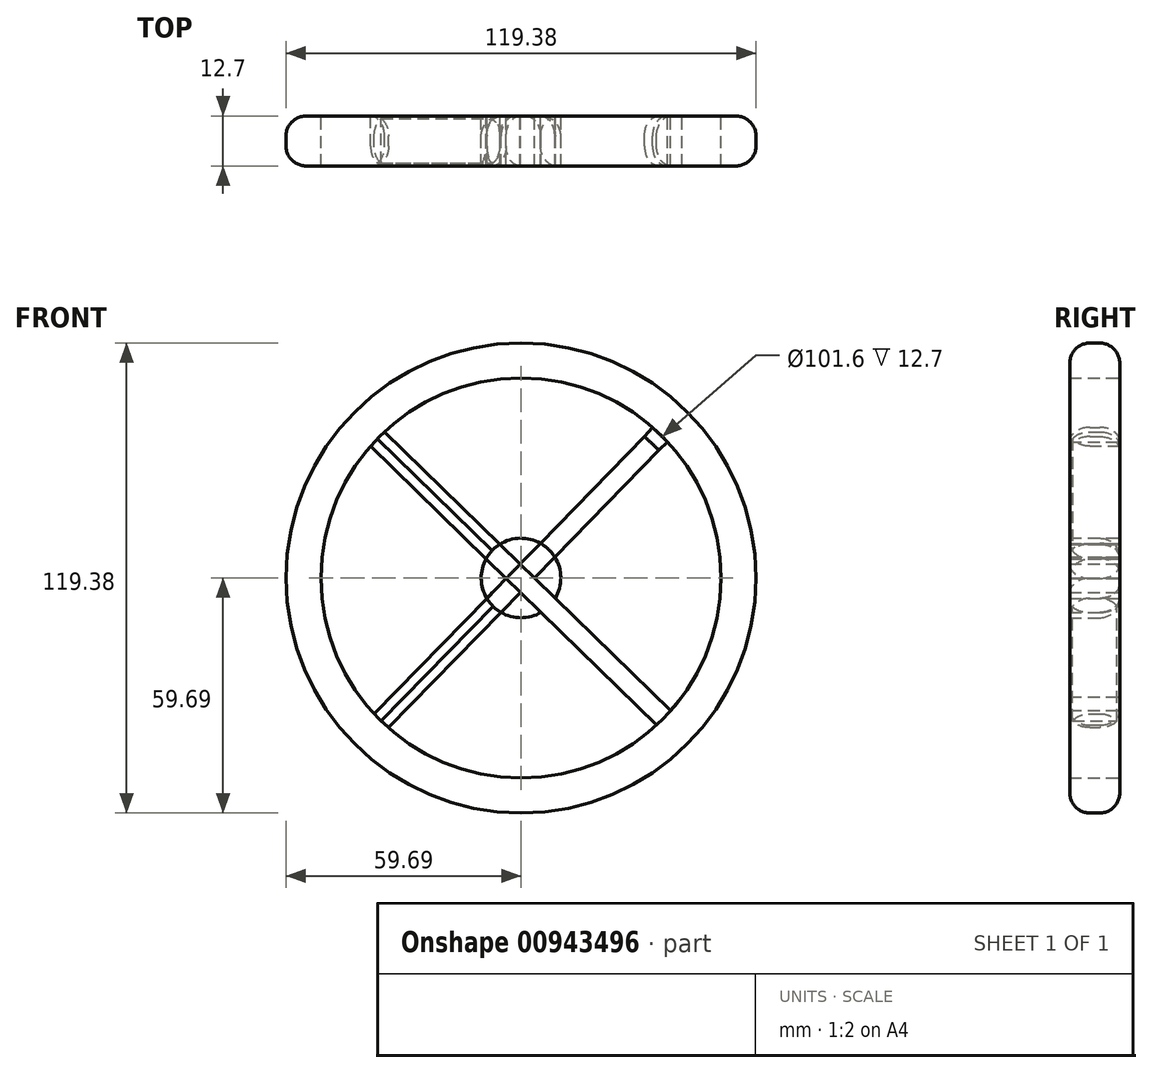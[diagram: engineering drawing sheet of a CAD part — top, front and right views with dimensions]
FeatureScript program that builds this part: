
annotation { "Feature Type Name" : "Feature", "Feature Type Description" : "" }
export const myFeature = defineFeature(function(context is Context, id is Id, definition is map)
    precondition{}
    {
        {
            var Q0;
            Q0=qCreatedBy(makeId("Front.planeOp"),FACE);
            var sketch = newSketch(context, id + "F0", { "sketchPlane" : qUnion([Q0])});
            skCircle(sketch, "E0", {"center": v(0, 0) * mm, "radius": 50.8 * mm});
            skCircle(sketch, "E1.0", {"center": v(0, 0) * mm, "radius": 59.7 * mm});
            skCircle(sketch, "E2", {"center": v(0, 0) * mm, "radius": 10.1 * mm});
            skLineSegment(sketch, "E3", {"start": v(37.18, 34.62) * mm, "end": v(-33.62, -38) * mm});
            skLineSegment(sketch, "E4", {"start": v(34.44, -37.34) * mm, "end": v(-38.2, 33.48) * mm});
            skLineSegment(sketch, "E5", {"start": v(31.36, 35.93) * mm, "end": v(-37.3, -34.5) * mm});
            skLineSegment(sketch, "E6", {"start": v(37.98, -33.7) * mm, "end": v(-34.67, 37.13) * mm});
            skLineSegment(sketch, "E7", {"start": v(-31.35, 38.6) * mm, "end": v(-34.67, 35.66) * mm});
            skLineSegment(sketch, "E8", {"start": v(40.85, -30.2) * mm, "end": v(37.98, -33.7) * mm});
            skLineSegment(sketch, "E9", {"start": v(37.02, 34.7) * mm, "end": v(37.18, 34.53) * mm});
            skLineSegment(sketch, "E10", {"start": v(-31.71, -39.69) * mm, "end": v(-35.52, -36.32) * mm});
            skPoint(sketch, "E11", {"position": v(-33.01, 37.13) * mm});
            skPoint(sketch, "E12", {"position": v(37.1, 34.62) * mm});
            skLineSegment(sketch, "E13", {"start": v(31.36, 35.93) * mm, "end": v(33.4, 38.27) * mm});
            skLineSegment(sketch, "E14", {"start": v(33.4, 38.27) * mm, "end": v(37.18, 34.62) * mm});
            skSolve(sketch);
        }
        {
            var Q0;
            Q0=makeQuery(id+"F0.imprint","IMPRINT",FACE,{"disambiguationData":[TD([[makeQuery(id+"F0.imprint","IMPRINT",EDGE,{"derivedFrom":sQuery(id+"F0.wireOp",EDGE,"E0")}),-1.0]])]});
            extrude(context, id + "F1", {"entities" : qUnion([Q0]), "endBound" : BoundingType.SYMMETRIC, "depth" : 12.7 * mm, "offsetDistance" : 25.4 * mm});
        }
        {
            var Q0;
            Q0=makeQuery(id+"F1.opExtrude","CAP_EDGE",EDGE,{"disambiguationData":[OSD([sQuery(id+"F0.wireOp",EDGE,"E1.0")])],"isStart":true});
            var Q1;
            Q1=makeQuery(id+"F1.opExtrude","CAP_EDGE",EDGE,{"disambiguationData":[OSD([sQuery(id+"F0.wireOp",EDGE,"E1.0")])],"isStart":false});
            fillet(context, id + "F2", {"entities" : qUnion([Q0, Q1]), "radius" : 5.08 * mm, "tangentPropagation" : true, "allowEdgeOverflow" : false});
        }
        {
            var Q0;
            Q0=makeQuery(id+"F0.imprint","IMPRINT",FACE,{"disambiguationData":[TD([[makeQuery(id+"F0.imprint","IMPRINT",EDGE,{"derivedFrom":sQuery(id+"F0.wireOp",EDGE,"E2")}),1.0]])]});
            extrude(context, id + "F3", {"entities" : qUnion([Q0]), "endBound" : BoundingType.SYMMETRIC, "depth" : 12.7 * mm, "offsetDistance" : 25.4 * mm});
        }
        {
            var Q0;
            Q0=makeQuery(id+"F3.opExtrude","CAP_EDGE",EDGE,{"disambiguationData":[OSD([sQuery(id+"F0.wireOp",EDGE,"E2")])],"isStart":true});
            fillet(context, id + "F4", {"entities" : qUnion([Q0]), "radius" : 5.08 * mm, "tangentPropagation" : true, "allowEdgeOverflow" : false});
        }
        {
            var Q0;
            {var subQ0=sQuery(id+"F0.wireOp",EDGE,"E8");Q0=makeQuery(id+"F0.imprint","IMPRINT",FACE,{"disambiguationData":[TD([[makeQuery(id+"F0.imprint","IMPRINT",EDGE,{"derivedFrom":subQ0}),1.0]])]});}
            var Q1;
            {var subQ0=sQuery(id+"F0.wireOp",EDGE,"E4");var subQ1=sQuery(id+"F0.wireOp",EDGE,"E2");var subQ2=makeQuery(id+"F0.imprint","INTERSECT",VERTEX,{"disambiguationData":[OD(1.0)],"derivedFrom":[subQ1,subQ0]});Q1=makeQuery(id+"F0.imprint","IMPRINT",FACE,{"disambiguationData":[TD([[makeQuery(id+"F0.imprint","IMPRINT",EDGE,{"disambiguationData":[TD([[subQ2,-1.0]])],"derivedFrom":subQ1}),1.0]])]});}
            var Q2;
            {var subQ0=sQuery(id+"F0.wireOp",EDGE,"E6");var subQ1=sQuery(id+"F0.wireOp",EDGE,"E3");var subQ2=makeQuery(id+"F0.imprint","INTERSECT",VERTEX,{"derivedFrom":[subQ1,subQ0]});Q2=makeQuery(id+"F0.imprint","IMPRINT",FACE,{"disambiguationData":[TD([[makeQuery(id+"F0.imprint","IMPRINT",EDGE,{"disambiguationData":[TD([[subQ2,-1.0]])],"derivedFrom":subQ1}),-1.0]])]});}
            var Q3;
            {var subQ0=sQuery(id+"F0.wireOp",EDGE,"E6");var subQ1=makeQuery(id+"F0.imprint","IMPRINT",VERTEX,{"derivedFrom":subQ0});Q3=makeQuery(id+"F0.imprint","IMPRINT",FACE,{"disambiguationData":[TD([[makeQuery(id+"F0.imprint","IMPRINT",EDGE,{"disambiguationData":[TD([[subQ1,1.0]])],"derivedFrom":subQ0}),1.0]])]});}
            var Q4;
            {var subQ0=sQuery(id+"F0.wireOp",EDGE,"E6");var subQ1=sQuery(id+"F0.wireOp",EDGE,"E2");var subQ2=makeQuery(id+"F0.imprint","INTERSECT",VERTEX,{"disambiguationData":[OD(0.0)],"derivedFrom":[subQ1,subQ0]});Q4=makeQuery(id+"F0.imprint","IMPRINT",FACE,{"disambiguationData":[TD([[makeQuery(id+"F0.imprint","IMPRINT",EDGE,{"disambiguationData":[TD([[subQ2,-1.0]])],"derivedFrom":subQ1}),1.0]])]});}
            var Q5;
            {var subQ0=sQuery(id+"F0.wireOp",EDGE,"E5");var subQ1=sQuery(id+"F0.wireOp",EDGE,"E0");var subQ2=makeQuery(id+"F0.imprint","INTERSECT",VERTEX,{"derivedFrom":[subQ1,subQ0]});Q5=makeQuery(id+"F0.imprint","IMPRINT",FACE,{"disambiguationData":[TD([[makeQuery(id+"F0.imprint","IMPRINT",EDGE,{"disambiguationData":[TD([[subQ2,-1.0]])],"derivedFrom":subQ1}),1.0]])]});}
            var Q6;
            {var subQ0=sQuery(id+"F0.wireOp",EDGE,"E5");var subQ1=sQuery(id+"F0.wireOp",EDGE,"E2");var subQ2=makeQuery(id+"F0.imprint","INTERSECT",VERTEX,{"disambiguationData":[OD(1.0)],"derivedFrom":[subQ1,subQ0]});Q6=makeQuery(id+"F0.imprint","IMPRINT",FACE,{"disambiguationData":[TD([[makeQuery(id+"F0.imprint","IMPRINT",EDGE,{"disambiguationData":[TD([[subQ2,-1.0]])],"derivedFrom":subQ1}),1.0]])]});}
            var Q7;
            {var subQ0=sQuery(id+"F0.wireOp",EDGE,"E13");Q7=makeQuery(id+"F0.imprint","IMPRINT",FACE,{"disambiguationData":[TD([[makeQuery(id+"F0.imprint","IMPRINT",EDGE,{"derivedFrom":subQ0}),-1.0]])]});}
            var Q8;
            {var subQ0=sQuery(id+"F0.wireOp",EDGE,"E5");var subQ1=sQuery(id+"F0.wireOp",EDGE,"E2");var subQ2=makeQuery(id+"F0.imprint","INTERSECT",VERTEX,{"disambiguationData":[OD(0.0)],"derivedFrom":[subQ1,subQ0]});Q8=makeQuery(id+"F0.imprint","IMPRINT",FACE,{"disambiguationData":[TD([[makeQuery(id+"F0.imprint","IMPRINT",EDGE,{"disambiguationData":[TD([[subQ2,1.0]])],"derivedFrom":subQ1}),1.0]])]});}
            extrude(context, id + "F5", {"entities" : qUnion([Q0, Q1, Q2, Q3, Q4, Q5, Q6, Q7, Q8]), "endBound" : BoundingType.SYMMETRIC, "depth" : 12.7 * mm, "offsetDistance" : 25.4 * mm});
        }
        {
            var Q0;
            {var subQ0=sQuery(id+"F0.wireOp",EDGE,"E4");var subQ1=makeQuery(id+"F0.imprint","INTERSECT",VERTEX,{"disambiguationData":[OD(1.0)],"derivedFrom":[sQuery(id+"F0.wireOp",EDGE,"E2"),subQ0]});Q0=makeQuery(id+"F5.opExtrude","CAP_EDGE",EDGE,{"disambiguationData":[OSD([subQ0]),TDD([makeQuery(id+"F0.imprint","IMPRINT",EDGE,{"disambiguationData":[TD([[makeQuery(id+"F0.imprint","INTERSECT",VERTEX,{"disambiguationData":[OD(0.0)],"derivedFrom":[sQuery(id+"F0.wireOp",EDGE,"E0"),subQ0]}),-1.0]])],"derivedFrom":subQ0}),makeQuery(id+"F0.imprint","IMPRINT",EDGE,{"disambiguationData":[TD([[subQ1,-1.0]])],"derivedFrom":subQ0})])],"isStart":false});}
            var Q1;
            {var subQ0=sQuery(id+"F0.wireOp",EDGE,"E3");var subQ1=makeQuery(id+"F0.imprint","INTERSECT",VERTEX,{"disambiguationData":[OD(1.0)],"derivedFrom":[sQuery(id+"F0.wireOp",EDGE,"E2"),subQ0]});Q1=makeQuery(id+"F5.opExtrude","CAP_EDGE",EDGE,{"disambiguationData":[OSD([subQ0]),TDD([makeQuery(id+"F0.imprint","IMPRINT",EDGE,{"disambiguationData":[TD([[subQ1,1.0]])],"derivedFrom":subQ0}),makeQuery(id+"F0.imprint","IMPRINT",EDGE,{"disambiguationData":[TD([[makeQuery(id+"F0.imprint","INTERSECT",VERTEX,{"derivedFrom":[subQ0,sQuery(id+"F0.wireOp",EDGE,"E10")]}),1.0]])],"derivedFrom":subQ0})])],"isStart":true});}
            var Q2;
            {var subQ0=sQuery(id+"F0.wireOp",EDGE,"E5");var subQ1=makeQuery(id+"F0.imprint","INTERSECT",VERTEX,{"disambiguationData":[OD(1.0)],"derivedFrom":[sQuery(id+"F0.wireOp",EDGE,"E2"),subQ0]});Q2=makeQuery(id+"F5.opExtrude","CAP_EDGE",EDGE,{"disambiguationData":[OSD([subQ0]),TDD([makeQuery(id+"F0.imprint","IMPRINT",EDGE,{"disambiguationData":[TD([[subQ1,1.0]])],"derivedFrom":subQ0}),makeQuery(id+"F0.imprint","IMPRINT",EDGE,{"disambiguationData":[TD([[makeQuery(id+"F0.imprint","INTERSECT",VERTEX,{"derivedFrom":[sQuery(id+"F0.wireOp",EDGE,"E0"),subQ0]}),1.0]])],"derivedFrom":subQ0})])],"isStart":false});}
            var Q3;
            {var subQ0=sQuery(id+"F0.wireOp",EDGE,"E5");var subQ1=makeQuery(id+"F0.imprint","INTERSECT",VERTEX,{"disambiguationData":[OD(0.0)],"derivedFrom":[sQuery(id+"F0.wireOp",EDGE,"E2"),subQ0]});Q3=makeQuery(id+"F5.opExtrude","CAP_EDGE",EDGE,{"disambiguationData":[OSD([subQ0]),TDD([makeQuery(id+"F0.imprint","IMPRINT",EDGE,{"disambiguationData":[TD([[makeQuery(id+"F0.imprint","INTERSECT",VERTEX,{"derivedFrom":[subQ0,sQuery(id+"F0.wireOp",EDGE,"E13")]}),-1.0]])],"derivedFrom":subQ0}),makeQuery(id+"F0.imprint","IMPRINT",EDGE,{"disambiguationData":[TD([[subQ1,-1.0]])],"derivedFrom":subQ0})])],"isStart":false});}
            var Q4;
            {var subQ0=sQuery(id+"F0.wireOp",EDGE,"E6");var subQ1=makeQuery(id+"F0.imprint","IMPRINT",VERTEX,{"derivedFrom":subQ0});var subQ2=makeQuery(id+"F0.imprint","INTERSECT",VERTEX,{"disambiguationData":[OD(0.0)],"derivedFrom":[sQuery(id+"F0.wireOp",EDGE,"E2"),subQ0]});Q4=makeQuery(id+"F5.opExtrude","CAP_EDGE",EDGE,{"disambiguationData":[OSD([subQ0]),TDD([makeQuery(id+"F0.imprint","IMPRINT",EDGE,{"disambiguationData":[TD([[subQ2,1.0]])],"derivedFrom":subQ0}),makeQuery(id+"F0.imprint","IMPRINT",EDGE,{"disambiguationData":[TD([[subQ1,1.0]])],"derivedFrom":subQ0}),makeQuery(id+"F0.imprint","IMPRINT",EDGE,{"disambiguationData":[TD([[subQ1,-1.0]])],"derivedFrom":subQ0})])],"isStart":false});}
            var Q5;
            {var subQ0=sQuery(id+"F0.wireOp",EDGE,"E4");var subQ1=makeQuery(id+"F0.imprint","INTERSECT",VERTEX,{"disambiguationData":[OD(0.0)],"derivedFrom":[sQuery(id+"F0.wireOp",EDGE,"E2"),subQ0]});Q5=makeQuery(id+"F5.opExtrude","CAP_EDGE",EDGE,{"disambiguationData":[OSD([subQ0]),TDD([makeQuery(id+"F0.imprint","IMPRINT",EDGE,{"disambiguationData":[TD([[subQ1,1.0]])],"derivedFrom":subQ0}),makeQuery(id+"F0.imprint","IMPRINT",EDGE,{"disambiguationData":[TD([[makeQuery(id+"F0.imprint","INTERSECT",VERTEX,{"disambiguationData":[OD(1.0)],"derivedFrom":[sQuery(id+"F0.wireOp",EDGE,"E0"),subQ0]}),1.0]])],"derivedFrom":subQ0})])],"isStart":false});}
            var Q6;
            {var subQ0=sQuery(id+"F0.wireOp",EDGE,"E4");var subQ1=makeQuery(id+"F0.imprint","INTERSECT",VERTEX,{"disambiguationData":[OD(1.0)],"derivedFrom":[sQuery(id+"F0.wireOp",EDGE,"E2"),subQ0]});Q6=makeQuery(id+"F5.opExtrude","CAP_EDGE",EDGE,{"disambiguationData":[OSD([subQ0]),TDD([makeQuery(id+"F0.imprint","IMPRINT",EDGE,{"disambiguationData":[TD([[makeQuery(id+"F0.imprint","INTERSECT",VERTEX,{"disambiguationData":[OD(0.0)],"derivedFrom":[sQuery(id+"F0.wireOp",EDGE,"E0"),subQ0]}),-1.0]])],"derivedFrom":subQ0}),makeQuery(id+"F0.imprint","IMPRINT",EDGE,{"disambiguationData":[TD([[subQ1,-1.0]])],"derivedFrom":subQ0})])],"isStart":true});}
            var Q7;
            {var subQ0=sQuery(id+"F0.wireOp",EDGE,"E5");var subQ1=makeQuery(id+"F0.imprint","INTERSECT",VERTEX,{"disambiguationData":[OD(0.0)],"derivedFrom":[sQuery(id+"F0.wireOp",EDGE,"E2"),subQ0]});Q7=makeQuery(id+"F5.opExtrude","CAP_EDGE",EDGE,{"disambiguationData":[OSD([subQ0]),TDD([makeQuery(id+"F0.imprint","IMPRINT",EDGE,{"disambiguationData":[TD([[makeQuery(id+"F0.imprint","INTERSECT",VERTEX,{"derivedFrom":[subQ0,sQuery(id+"F0.wireOp",EDGE,"E13")]}),-1.0]])],"derivedFrom":subQ0}),makeQuery(id+"F0.imprint","IMPRINT",EDGE,{"disambiguationData":[TD([[subQ1,-1.0]])],"derivedFrom":subQ0})])],"isStart":true});}
            var Q8;
            {var subQ0=sQuery(id+"F0.wireOp",EDGE,"E6");var subQ1=makeQuery(id+"F0.imprint","IMPRINT",VERTEX,{"derivedFrom":subQ0});var subQ2=makeQuery(id+"F0.imprint","INTERSECT",VERTEX,{"disambiguationData":[OD(0.0)],"derivedFrom":[sQuery(id+"F0.wireOp",EDGE,"E2"),subQ0]});Q8=makeQuery(id+"F5.opExtrude","CAP_EDGE",EDGE,{"disambiguationData":[OSD([subQ0]),TDD([makeQuery(id+"F0.imprint","IMPRINT",EDGE,{"disambiguationData":[TD([[subQ2,1.0]])],"derivedFrom":subQ0}),makeQuery(id+"F0.imprint","IMPRINT",EDGE,{"disambiguationData":[TD([[subQ1,1.0]])],"derivedFrom":subQ0}),makeQuery(id+"F0.imprint","IMPRINT",EDGE,{"disambiguationData":[TD([[subQ1,-1.0]])],"derivedFrom":subQ0})])],"isStart":true});}
            var Q9;
            {var subQ0=sQuery(id+"F0.wireOp",EDGE,"E3");var subQ1=makeQuery(id+"F0.imprint","INTERSECT",VERTEX,{"disambiguationData":[OD(1.0)],"derivedFrom":[sQuery(id+"F0.wireOp",EDGE,"E2"),subQ0]});Q9=makeQuery(id+"F5.opExtrude","CAP_EDGE",EDGE,{"disambiguationData":[OSD([subQ0]),TDD([makeQuery(id+"F0.imprint","IMPRINT",EDGE,{"disambiguationData":[TD([[subQ1,1.0]])],"derivedFrom":subQ0}),makeQuery(id+"F0.imprint","IMPRINT",EDGE,{"disambiguationData":[TD([[makeQuery(id+"F0.imprint","INTERSECT",VERTEX,{"derivedFrom":[subQ0,sQuery(id+"F0.wireOp",EDGE,"E10")]}),1.0]])],"derivedFrom":subQ0})])],"isStart":false});}
            fillet(context, id + "F6", {"entities" : qUnion([Q0, Q1, Q2, Q3, Q4, Q5, Q6, Q7, Q8, Q9]), "radius" : 5.08 * mm, "tangentPropagation" : true, "allowEdgeOverflow" : false});
        }
    });
